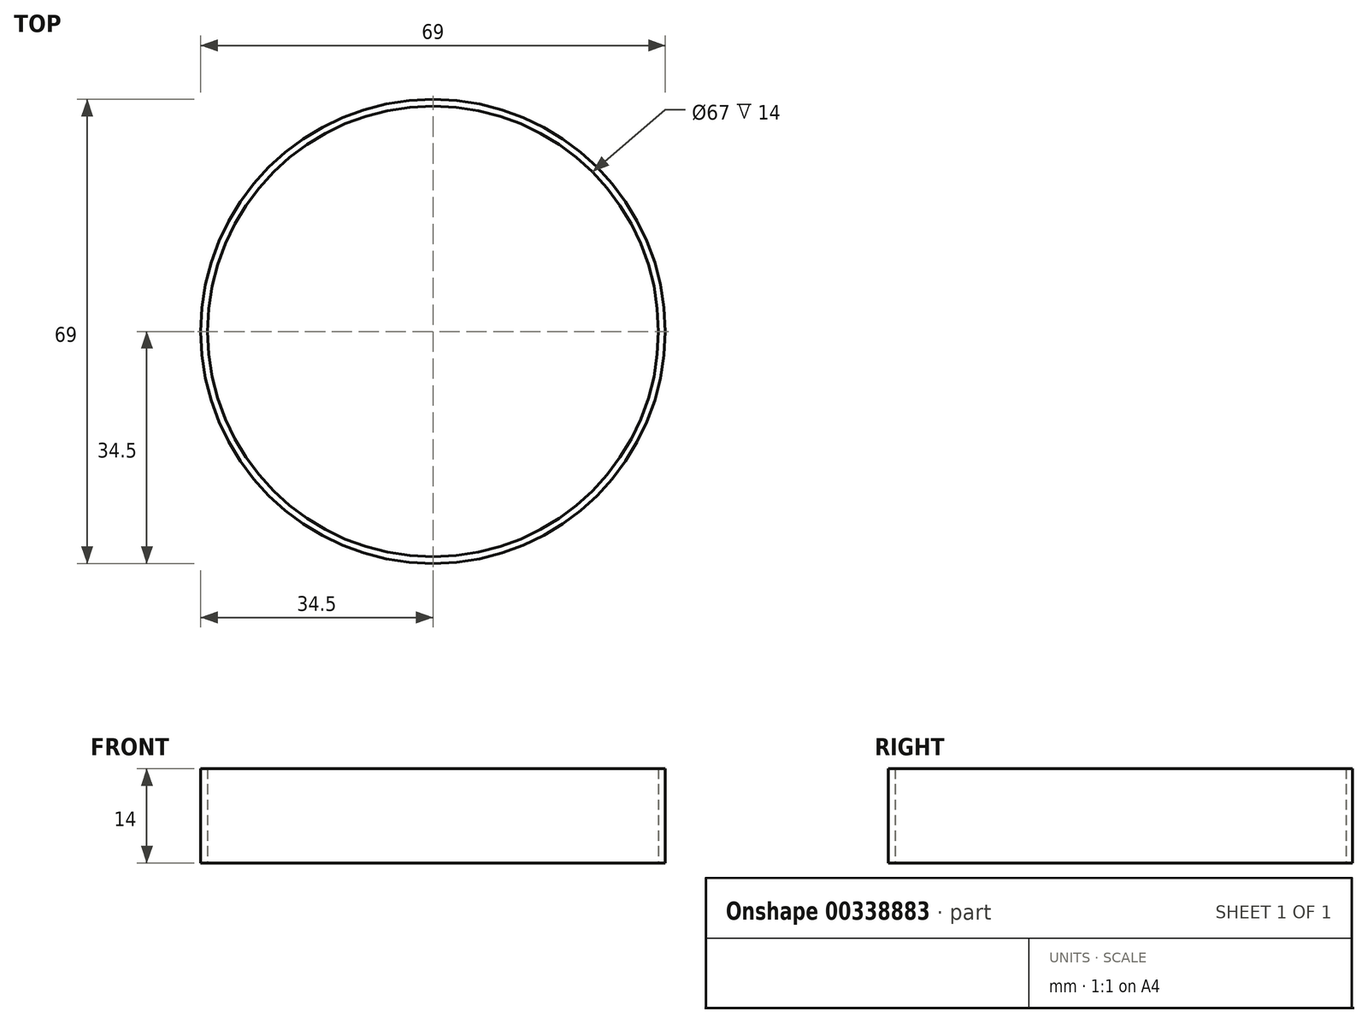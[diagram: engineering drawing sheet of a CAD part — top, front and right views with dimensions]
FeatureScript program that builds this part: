
annotation { "Feature Type Name" : "Feature", "Feature Type Description" : "" }
export const myFeature = defineFeature(function(context is Context, id is Id, definition is map)
    precondition{}
    {
        {
            var Q0;
            Q0=qCreatedBy(makeId("Top.planeOp"),FACE);
            var sketch = newSketch(context, id + "F0", { "sketchPlane" : qUnion([Q0])});
            skCircle(sketch, "E0", {"center": v(0, 0) * mm, "radius": 33.5 * mm});
            skCircle(sketch, "E1.0", {"center": v(0, 0) * mm, "radius": 34.5 * mm});
            skSolve(sketch);
        }
        {
            var Q0;
            Q0=makeQuery(id+"F0.imprint","IMPRINT",FACE,{"disambiguationData":[TD([[makeQuery(id+"F0.imprint","IMPRINT",EDGE,{"derivedFrom":sQuery(id+"F0.wireOp",EDGE,"E0")}),-1.0]])]});
            extrude(context, id + "F1", {"entities" : qUnion([Q0]), "depth" : 14 * mm});
        }
    });
